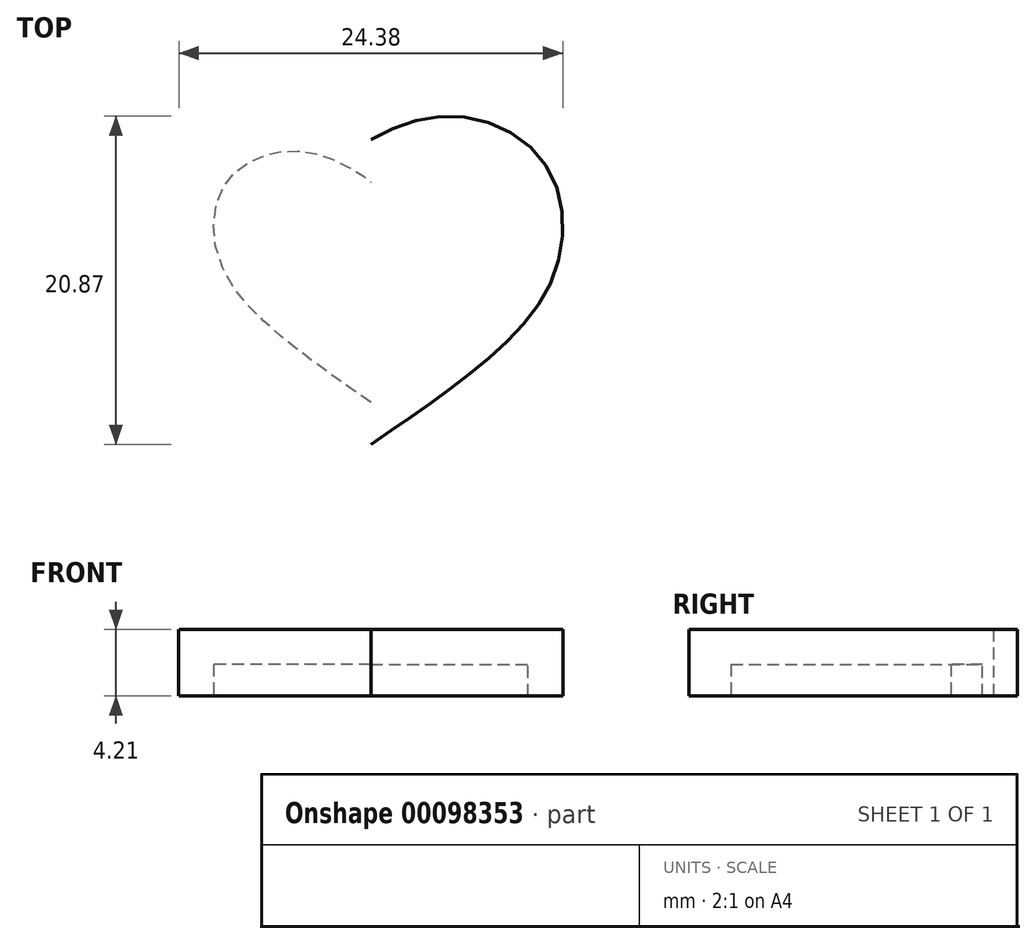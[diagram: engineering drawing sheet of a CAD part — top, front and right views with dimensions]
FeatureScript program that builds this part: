
annotation { "Feature Type Name" : "Feature", "Feature Type Description" : "" }
export const myFeature = defineFeature(function(context is Context, id is Id, definition is map)
    precondition{}
    {
        {
            var Q0;
            Q0=qCreatedBy(makeId("Top.planeOp"),FACE);
            var sketch = newSketch(context, id + "F0", { "sketchPlane" : qUnion([Q0])});
            skFitSpline(sketch, "E0", {"points": [v(-4.37, -12.85) * mm, v(-9.6, -9.04) * mm, v(-13.84, -4.2) * mm, v(-13.7, 0.88) * mm, v(-10.45, 3) * mm, v(-6.8, 2.57) * mm, v(-4.36, 1.09) * mm, v(-4.37, 0.98) * mm], "startDerivative": vector(-33.02, 22.7) * mm, "endDerivative": vector(-1.9, -3.3) * mm});
            skFitSpline(sketch, "E1.MirrorCS", {"points": [v(-4.37, -12.85) * mm, v(0.86, -9.04) * mm, v(5.1, -4.2) * mm, v(4.97, 0.88) * mm, v(1.7, 3) * mm, v(-1.94, 2.57) * mm, v(-4.38, 1.09) * mm, v(-4.37, 0.98) * mm], "startDerivative": vector(33.02, 22.7) * mm, "endDerivative": vector(1.9, -3.3) * mm});
            skSolve(sketch);
        }
        {
            var Q0;
            Q0 = qSketchRegion(id + "F0", true);
            extrude(context, id + "F1", {"entities" : qUnion([Q0]), "depth" : 2 * mm});
        }
        {
            var Q0;
            Q0=makeQuery(id+"F1.opExtrude","CAP_FACE",FACE,{"disambiguationData":[OSD([sQuery(id+"F0.wireOp",EDGE,"E0"),sQuery(id+"F0.wireOp",EDGE,"E1.MirrorCS")])],"isStart":true});
            shell(context, id + "F2", {"entities" : qUnion([Q0]), "thickness" : 2.2 * mm, "oppositeDirection" : true});
        }
    });
